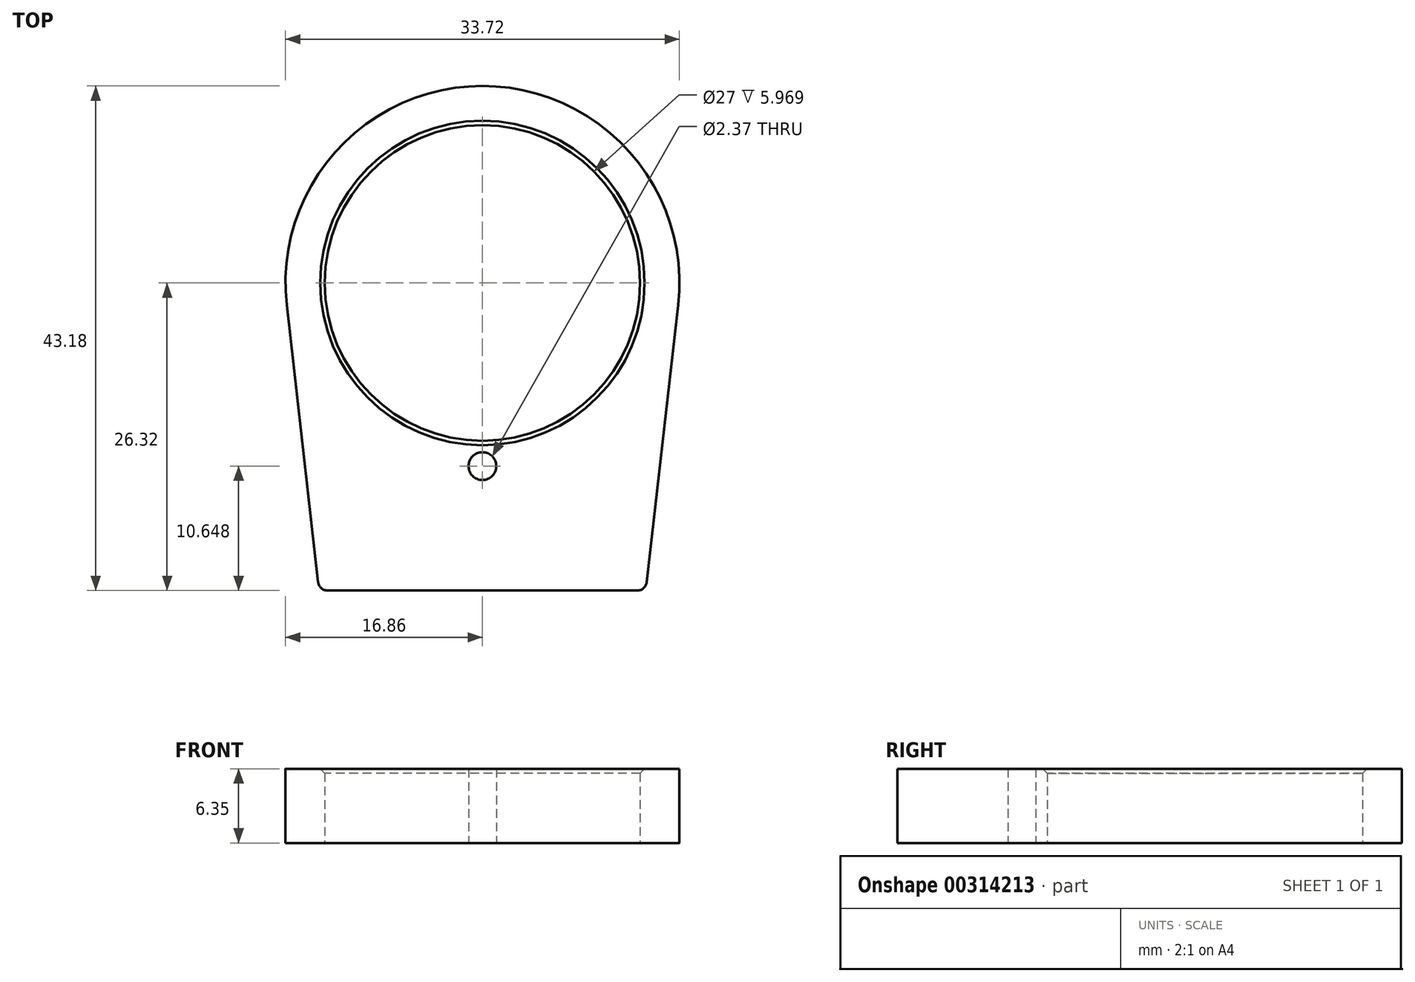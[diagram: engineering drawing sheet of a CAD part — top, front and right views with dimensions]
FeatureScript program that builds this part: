
annotation { "Feature Type Name" : "Feature", "Feature Type Description" : "" }
export const myFeature = defineFeature(function(context is Context, id is Id, definition is map)
    precondition{}
    {
        {
            var Q0;
            Q0=qCreatedBy(makeId("Top.planeOp"),FACE);
            var sketch = newSketch(context, id + "F0", { "sketchPlane" : qUnion([Q0])});
            skCircle(sketch, "E0", {"center": v(0, 0) * mm, "radius": 13.5 * mm});
            skArc(sketch, "E1", {"start": v(16.75, -1.9) * mm, "mid": v(0, 16.86) * mm, "end": v(-16.75, -1.9) * mm});
            skLineSegment(sketch, "E2", {"start": v(-13.25, -26.32) * mm, "end": v(0, -26.32) * mm});
            skLineSegment(sketch, "E3", {"start": v(-16.75, -1.9) * mm, "end": v(-14.06, -25.6) * mm});
            skPoint(sketch, "E4", {"position": v(0, -26.32) * mm});
            skLineSegment(sketch, "E5.MirrorCS", {"start": v(13.25, -26.32) * mm, "end": v(0, -26.32) * mm});
            skLineSegment(sketch, "E6.MirrorCS", {"start": v(16.75, -1.9) * mm, "end": v(14.06, -25.6) * mm});
            skCircle(sketch, "E7", {"center": v(0, -15.67) * mm, "radius": 1.19 * mm});
            skPoint(sketch, "E8.visualSharp", {"position": v(-13.98, -26.32) * mm});
            skArc(sketch, "E8.filletArc", {"start": v(-14.06, -25.6) * mm, "mid": v(-13.8, -26.11) * mm, "end": v(-13.25, -26.32) * mm});
            skPoint(sketch, "E9.visualSharp", {"position": v(13.98, -26.32) * mm});
            skArc(sketch, "E9.filletArc", {"start": v(13.25, -26.32) * mm, "mid": v(13.8, -26.11) * mm, "end": v(14.06, -25.6) * mm});
            skSolve(sketch);
        }
        {
            var Q0;
            Q0=makeQuery(id+"F0.imprint","IMPRINT",FACE,{"disambiguationData":[TD([[makeQuery(id+"F0.imprint","IMPRINT",EDGE,{"derivedFrom":sQuery(id+"F0.wireOp",EDGE,"E0")}),-1.0]])]});
            extrude(context, id + "F1", {"entities" : qUnion([Q0]), "depth" : 6.35 * mm});
        }
        {
            var Q0;
            Q0=makeQuery(id+"F1.opExtrude","CAP_EDGE",EDGE,{"disambiguationData":[OSD([sQuery(id+"F0.wireOp",EDGE,"E0")])],"isStart":false});
            chamfer(context, id + "F2", {"entities" : qUnion([Q0]), "width" : 0.38 * mm, "tangentPropagation" : true});
        }
    });
